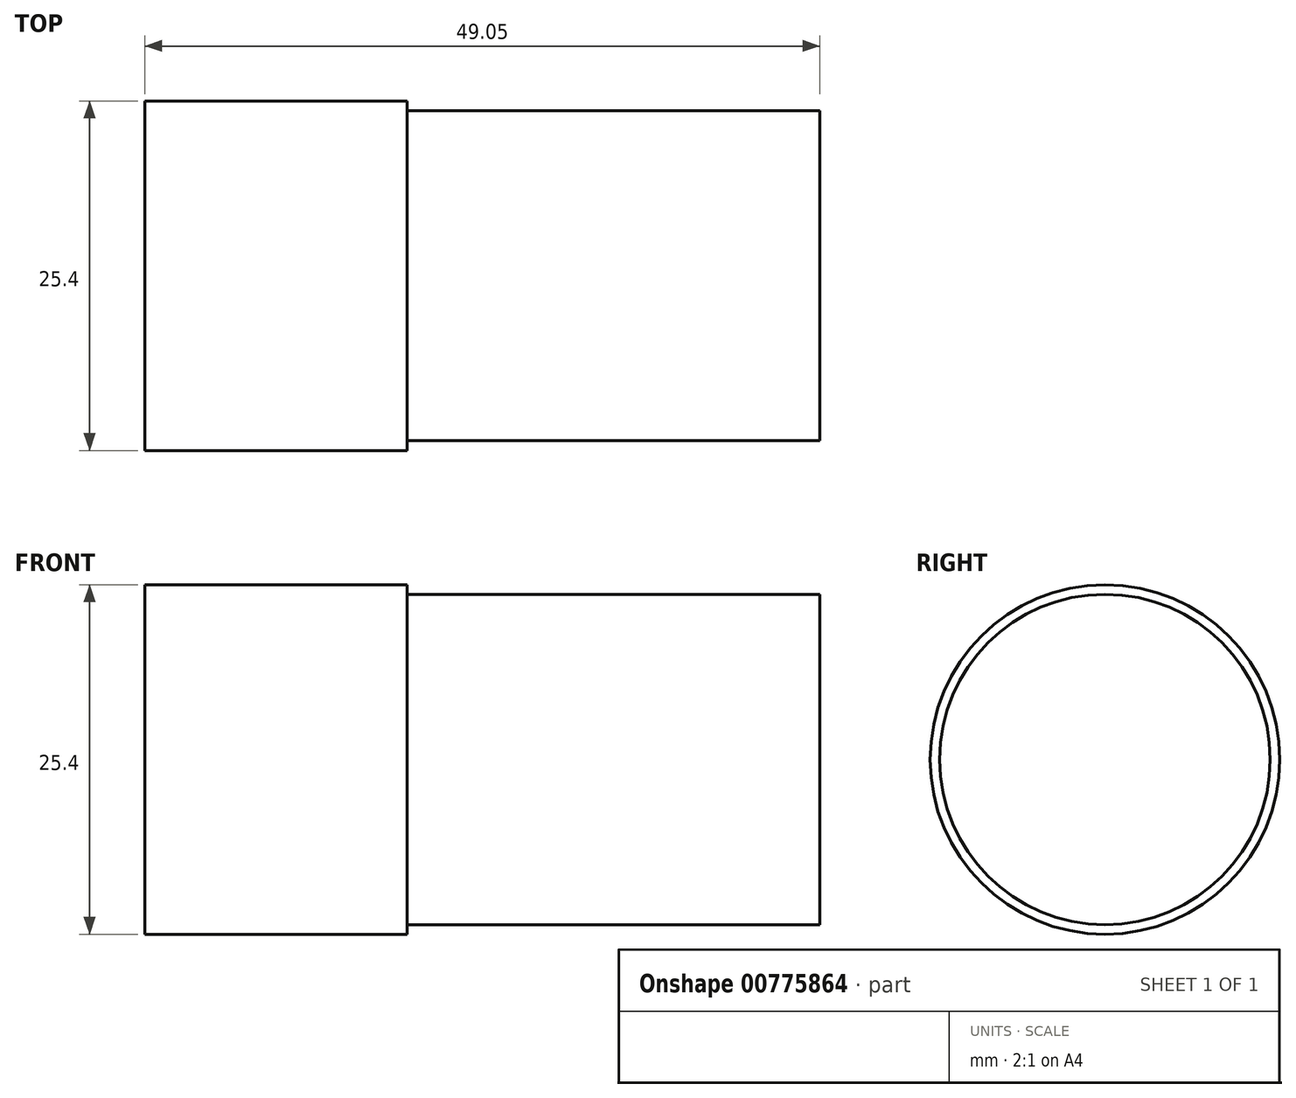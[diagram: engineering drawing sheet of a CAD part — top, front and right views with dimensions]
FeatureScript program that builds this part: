
annotation { "Feature Type Name" : "Feature", "Feature Type Description" : "" }
export const myFeature = defineFeature(function(context is Context, id is Id, definition is map)
    precondition{}
    {
        {
            var Q0;
            Q0=qCreatedBy(makeId("Front.planeOp"),FACE);
            var sketch = newSketch(context, id + "F0", { "sketchPlane" : qUnion([Q0])});
            skLineSegment(sketch, "E0.bottom", {"start": v(0, 0) * mm, "end": v(19.05, 0) * mm});
            skLineSegment(sketch, "E0.top", {"start": v(0, 12.7) * mm, "end": v(19.05, 12.7) * mm});
            skLineSegment(sketch, "E0.left", {"start": v(0, 0) * mm, "end": v(0, 12.7) * mm});
            skLineSegment(sketch, "E0.right", {"start": v(19.05, 0) * mm, "end": v(19.05, 12.7) * mm});
            skLineSegment(sketch, "E1.bottom", {"start": v(19.05, 0) * mm, "end": v(49.05, 0) * mm});
            skLineSegment(sketch, "E1.top", {"start": v(19.05, 12) * mm, "end": v(49.05, 12) * mm});
            skLineSegment(sketch, "E1.left", {"start": v(19.05, 0) * mm, "end": v(19.05, 12) * mm});
            skLineSegment(sketch, "E1.right", {"start": v(49.05, 0) * mm, "end": v(49.05, 12) * mm});
            skSolve(sketch);
        }
        {
            var Q0;
            Q0 = qSketchRegion(id + "F0", true);
            var Q1;
            Q1=sQuery(id+"F0.wireOp",EDGE,"E1.bottom");
            revolve(context, id + "F1", {"surfaceOperationType" : NewSurfaceOperationType.NEW, "entities" : qUnion([Q0]), "axis" : qUnion([Q1]), "revolveType" : RevolveType.FULL});
        }
    });
